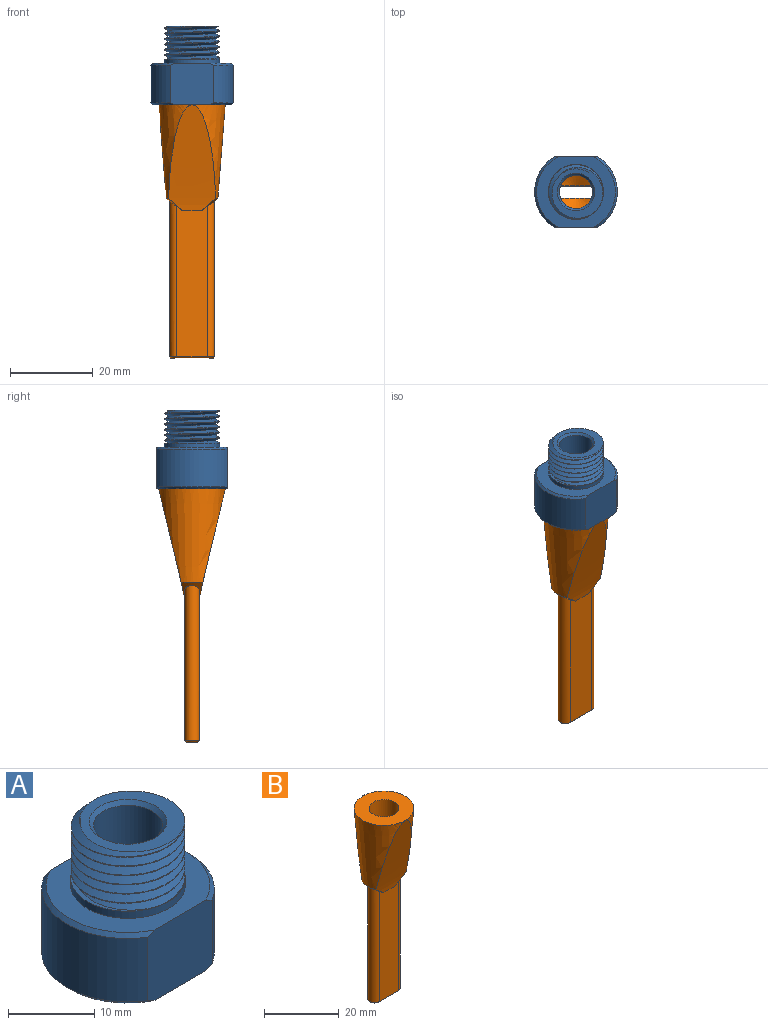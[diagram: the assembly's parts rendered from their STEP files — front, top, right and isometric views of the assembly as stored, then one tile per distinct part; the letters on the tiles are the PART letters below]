
ASSEMBLY  parts=2 mates=1
PART A: 21 faces, bbox 20x17.9x19.8 mm
  f0: plane 0.34x0.29mm, normal (0,1,0), area 0mm2, adj f11,f12,f13
  f1: cylinder r=6.58mm len=13.17mm, axis (0,0,1), area 25.1mm2, adj f6,f10,f11,f12,f14
  f2: cylinder r=10mm len=17mm, axis (0,0,1), area 182.9mm2, adj f7,f8,f17,f19
  f3: cylinder r=10mm len=17mm, axis (0,0,1), area 182.9mm2, adj f7,f8,f16,f18
  f4: plane 19x17mm, normal (0,0,1), area 133.2mm2, adj f7,f8,f15,f18,f19
  f5: plane 19x17mm, normal (0,0,-1), area 221.8mm2, adj f7,f8,f9,f16,f17
  f6: plane 12.25x12.24mm, normal (0,0,1), area 53.8mm2, adj f1,f11,f12,f20
  f7: plane 10.57x10.04mm, normal (0,-1,0), area 104.4mm2, adj f2,f3,f4,f5,f16,f17,f18,f19
  f8: plane 10.57x10.04mm, normal (0,1,0), area 104.4mm2, adj f2,f3,f4,f5,f16,f17,f18,f19
  f9: cylinder r=4mm len=18.5mm, axis (0,0,1), area 465mm2, adj f5,f20
  f10: plane 0.48x0.28mm, normal (0,1,0), area 0.1mm2, adj f1,f12,f14
  f11: bspline ~15.21x13.17mm, area 285.1mm2, adj f0,f1,f6,f12,f13,f14
  f12: bspline ~15.21x13.17mm, area 281.4mm2, adj f0,f1,f6,f10,f11,f13,f14
  f13: cylinder r=5.84mm len=10.05mm, axis (0,0,-1), area 3.1mm2, adj f0,f11,f12,f14
  f14: plane 13.33x13.33mm, normal (0,0,1), area 18mm2, adj f1,f10,f11,f12,f13,f15
  f15: cylinder r=6.65mm len=13.3mm, axis (0,0,-1), area 41.8mm2, adj f4,f14
  f16: cone r=10mm half-angle=45deg, axis (0,0,1), area 14.6mm2, adj f3,f5,f7,f8
  f17: cone r=10mm half-angle=45deg, axis (0,0,1), area 14.6mm2, adj f2,f5,f7,f8
  f18: cone r=9.5mm half-angle=45deg, axis (0,0,-1), area 14.6mm2, adj f3,f4,f7,f8
  f19: cone r=9.5mm half-angle=45deg, axis (0,0,-1), area 14.6mm2, adj f2,f4,f7,f8
  f20: cone r=4mm half-angle=45deg, axis (0,0,1), area 18.9mm2, adj f6,f9
PART B: 29 faces, bbox 16.1x16.1x61.1 mm
  f0: cylinder r=1.5mm len=53mm, axis (0,0,-1), area 249.7mm2, adj f1,f3,f10,f17,f19,f20,f21,f26
  f1: plane 52.84x7mm, normal (0,-1,0), area 364mm2, adj f0,f2,f19,f26
  f2: cylinder r=1.5mm len=53mm, axis (0,0,-1), area 249.7mm2, adj f1,f3,f4,f16,f18,f19,f20,f26
  f3: plane 52.84x7mm, normal (0,1,0), area 364mm2, adj f0,f2,f20,f27
  f4: plane 2.97x1.29mm, normal (0,0,-1), area 2.3mm2, adj f2,f28
  f5: plane 4.87x0.3mm, normal (0,0,-1), area 1.4mm2, adj f7,f8,f14,f24
  f6: cone r=8mm half-angle=4.5deg, axis (0,0,1), area 567.6mm2, adj f7,f8,f11,f22,f23,f24,f25
  f7: cone r=6.23mm half-angle=47.2deg, axis (0,0,1), area 10.8mm2, adj f5,f6,f9,f12,f14,f15,f22,f24
  f8: cone r=6.23mm half-angle=47.2deg, axis (0,0,1), area 10.8mm2, adj f5,f6,f9,f12,f13,f14,f22,f24
  f9: plane 4.87x0.3mm, normal (0,0,-1), area 1.4mm2, adj f7,f8,f12,f22
  f10: plane 2.7x0.92mm, normal (0,0,-1), area 0.2mm2, adj f0,f21
  f11: plane 16x16mm, normal (0,0,1), area 150.8mm2, adj f6,f28
  f12: plane 36.25x7.35mm, normal (0,1,0), area 256.3mm2, adj f7,f8,f9,f13,f15,f19
  f13: cylinder r=1.75mm len=37.4mm, axis (0,0,1), area 203.2mm2, adj f8,f12,f14,f18
  f14: plane 36.25x7.35mm, normal (0,-1,0), area 256.3mm2, adj f5,f7,f8,f13,f15,f20
  f15: cylinder r=1.75mm len=37.4mm, axis (0,0,1), area 203.2mm2, adj f7,f12,f14,f21
  f16: plane 2.7x0.92mm, normal (0,0,-1), area 0.2mm2, adj f2,f18
  f17: plane 2.97x1.29mm, normal (0,0,-1), area 2.3mm2, adj f0,f28
  f18: cone r=1.45mm half-angle=45deg, axis (0,0,1), area 2.1mm2, adj f2,f13,f16,f19,f20
  f19: plane 7.25x0.26mm, normal (0,0.71,-0.71), area 2.6mm2, adj f0,f1,f2,f12,f18,f21
  f20: plane 7.25x0.26mm, normal (0,-0.71,-0.71), area 2.6mm2, adj f0,f2,f3,f14,f18,f21
  f21: cone r=1.75mm half-angle=45deg, axis (0,0,1), area 2.1mm2, adj f0,f10,f15,f19,f20
  f22: extruded ~25.5x11.33mm, area 225.7mm2, adj f6,f7,f8,f9,f23
  f23: plane 0.08x0mm, normal (0,-1,0), area 0mm2, adj f6,f22
  f24: extruded ~25.5x11.33mm, area 225.7mm2, adj f5,f6,f7,f8,f25
  f25: plane 0.08x0mm, normal (0,1,0), area 0mm2, adj f6,f24
  f26: cone r=0mm half-angle=59deg, axis (0,0,1), area 15.7mm2, adj f0,f1,f2,f28
  f27: cone r=0mm half-angle=59deg, axis (0,0,1), area 15.7mm2, adj f0,f2,f3,f28
  f28: cylinder r=4mm len=8mm, axis (0,0,1), area 201.1mm2, adj f4,f11,f17,f26,f27
PLACE A t=(-10.87,-8.42,-70.78)mm
PLACE B t=(-10.87,-8.42,-44.79)mm
MATE fastened A.f1 <-> B.f6  axis (0,0,-1) through (-10.87,-8.42,-29.19)mm
